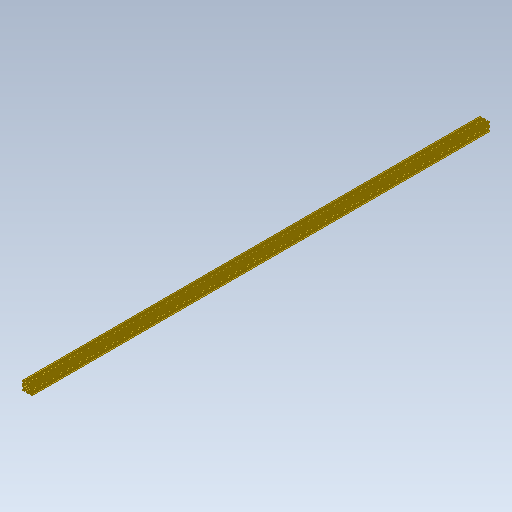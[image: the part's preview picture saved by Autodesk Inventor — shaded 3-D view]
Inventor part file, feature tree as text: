
AUTODESK INVENTOR PART (.ipt)
format: ipt  version: 2025.2 (Build 292293000, 293)  size: 402,944 bytes
history: native  units: mm
features: mirror x2, other x1, extrude x1, fillet x1, sketch x1
ambient origin geometry x8: Origin, YZ Plane, XZ Plane, XY Plane, X Axis, Y Axis, Z Axis, Center Point
bodies: Body1 (feature_tree)
feature tree (6):
  other  "Sólido1"
  extrude  "Extrusão1"  Depth=20.0mm
  mirror  "Espelhar1"
  mirror  "Espelhar2"
  fillet  "Arredondamento1"  Radius=6.2mm
  sketch  "Esboço1"  dims[d1=40.0mm d2=20.0mm d3=6.2mm d4=20.0mm d5=6.0mm d7=2.0mm d9=5.0mm d10=10.0mm d14=6.0mm d15=0.5mm d16=0.5mm d19=4.0mm d20=0.694219mm d21=1.0mm d24=0.695838mm d25=2000.0mm d26=0.0mm d27=1.0mm]
